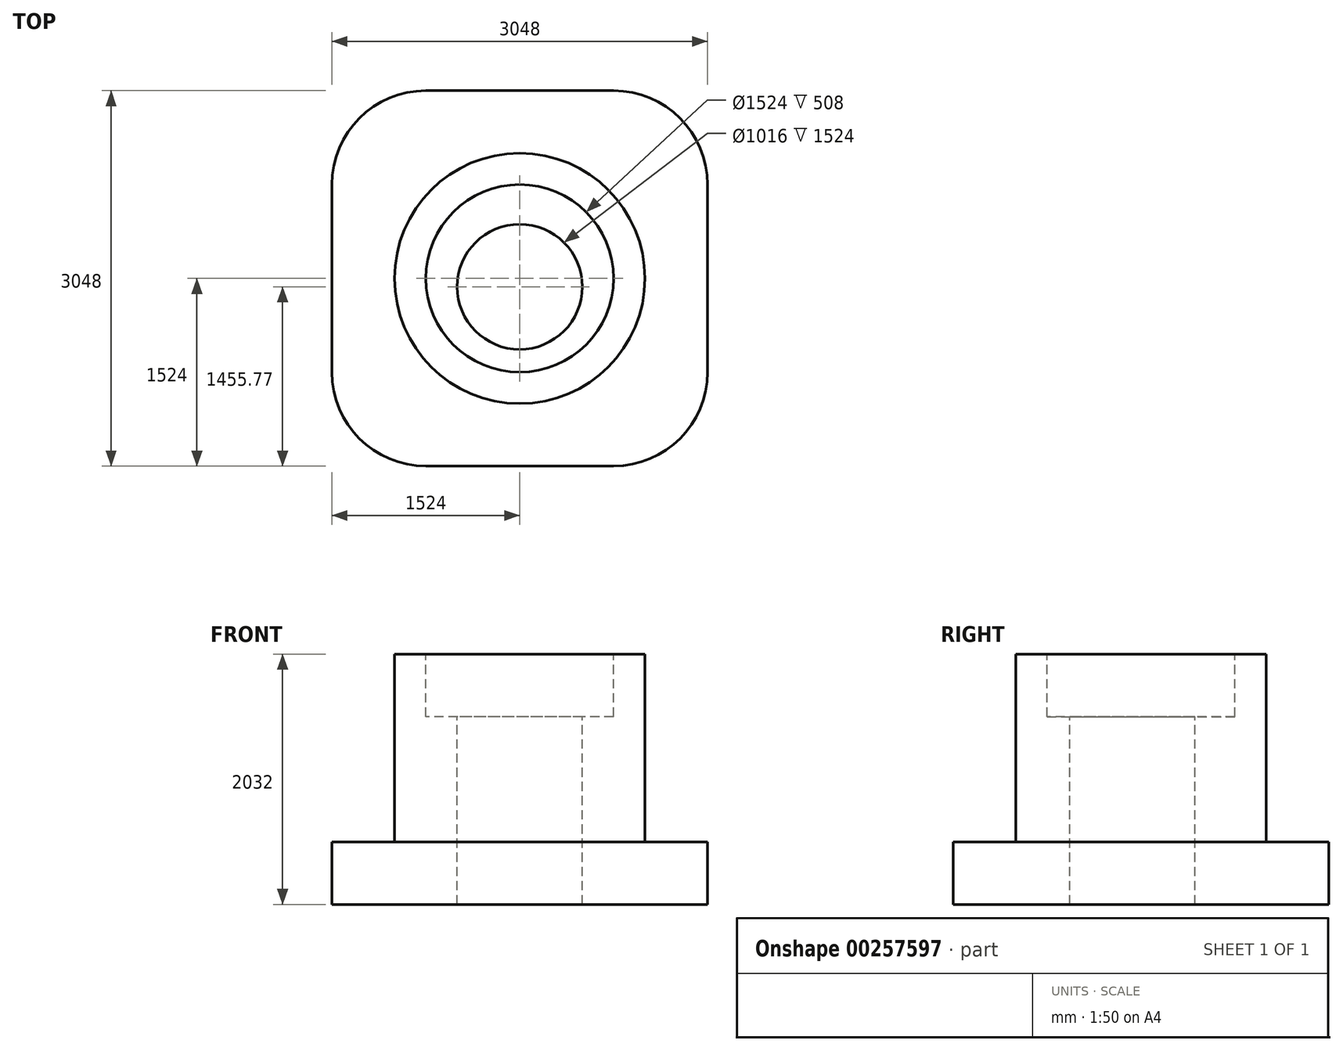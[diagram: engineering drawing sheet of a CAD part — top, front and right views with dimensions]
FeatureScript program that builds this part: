
annotation { "Feature Type Name" : "Feature", "Feature Type Description" : "" }
export const myFeature = defineFeature(function(context is Context, id is Id, definition is map)
    precondition{}
    {
        {
            var Q0;
            Q0=qCreatedBy(makeId("Top.planeOp"),FACE);
            var sketch = newSketch(context, id + "F0", { "sketchPlane" : qUnion([Q0])});
            skLineSegment(sketch, "E0.bottom", {"start": v(762, -1524) * mm, "end": v(-762, -1524) * mm});
            skLineSegment(sketch, "E0.top", {"start": v(762, 1524) * mm, "end": v(-762, 1524) * mm});
            skLineSegment(sketch, "E0.left", {"start": v(1524, -762) * mm, "end": v(1524, 762) * mm});
            skLineSegment(sketch, "E0.right", {"start": v(-1524, -762) * mm, "end": v(-1524, 762) * mm});
            skPoint(sketch, "E0.middle", {"position": v(0, 0) * mm});
            skPoint(sketch, "E1.visualSharp", {"position": v(-1524, 1524) * mm});
            skArc(sketch, "E1.filletArc", {"start": v(-762, 1524) * mm, "mid": v(-1300.82, 1300.82) * mm, "end": v(-1524, 762) * mm});
            skPoint(sketch, "E2.visualSharp", {"position": v(1524, 1524) * mm});
            skArc(sketch, "E2.filletArc", {"start": v(1524, 762) * mm, "mid": v(1300.82, 1300.82) * mm, "end": v(762, 1524) * mm});
            skPoint(sketch, "E3.visualSharp", {"position": v(1524, -1524) * mm});
            skArc(sketch, "E3.filletArc", {"start": v(762, -1524) * mm, "mid": v(1300.82, -1300.82) * mm, "end": v(1524, -762) * mm});
            skPoint(sketch, "E4.visualSharp", {"position": v(-1524, -1524) * mm});
            skArc(sketch, "E4.filletArc", {"start": v(-1524, -762) * mm, "mid": v(-1300.82, -1300.82) * mm, "end": v(-762, -1524) * mm});
            skSolve(sketch);
        }
        {
            var Q0;
            Q0=makeQuery(id+"F0.imprint","IMPRINT",FACE,{"disambiguationData":[TD([[makeQuery(id+"F0.imprint","IMPRINT",EDGE,{"derivedFrom":sQuery(id+"F0.wireOp",EDGE,"E0.bottom")}),-1.0]])]});
            extrude(context, id + "F1", {"entities" : qUnion([Q0]), "oppositeDirection" : true, "depth" : 508 * mm});
        }
        {
            var Q0;
            Q0=makeQuery(id+"F1.opExtrude","CAP_FACE",FACE,{"disambiguationData":[OSD([sQuery(id+"F0.wireOp",EDGE,"E0.bottom"),sQuery(id+"F0.wireOp",EDGE,"E0.top"),sQuery(id+"F0.wireOp",EDGE,"E0.left"),sQuery(id+"F0.wireOp",EDGE,"E0.right"),sQuery(id+"F0.wireOp",EDGE,"E1.filletArc"),sQuery(id+"F0.wireOp",EDGE,"E2.filletArc"),sQuery(id+"F0.wireOp",EDGE,"E3.filletArc"),sQuery(id+"F0.wireOp",EDGE,"E4.filletArc")])],"isStart":true});
            var sketch = newSketch(context, id + "F2", { "sketchPlane" : qUnion([Q0])});
            skCircle(sketch, "E5", {"center": v(0, 0) * mm, "radius": 1016 * mm});
            skSolve(sketch);
        }
        {
            var Q0;
            Q0 = qSketchRegion(id + "F2", true);
            extrude(context, id + "F3", {"entities" : qUnion([Q0]), "operationType" : NewBodyOperationType.ADD, "depth" : 1524 * mm});
        }
        {
            var Q0;
            Q0=makeQuery(id+"F3.opExtrude","CAP_FACE",FACE,{"disambiguationData":[OSD([sQuery(id+"F2.wireOp",EDGE,"E5")])],"isStart":false});
            var sketch = newSketch(context, id + "F4", { "sketchPlane" : qUnion([Q0])});
            skCircle(sketch, "E6", {"center": v(0, 0) * mm, "radius": 762 * mm});
            skSolve(sketch);
        }
        {
            var Q0;
            Q0 = qSketchRegion(id + "F4", true);
            extrude(context, id + "F5", {"entities" : qUnion([Q0]), "operationType" : NewBodyOperationType.REMOVE, "oppositeDirection" : true, "depth" : 508 * mm});
        }
        {
            var Q0;
            Q0=makeQuery(id+"F5.boolean.opBoolean","COPY",FACE,{"derivedFrom":makeQuery(id+"F5.opExtrude","CAP_FACE",FACE,{"disambiguationData":[OSD([sQuery(id+"F4.wireOp",EDGE,"E6")])],"isStart":false})});
            var sketch = newSketch(context, id + "F6", { "sketchPlane" : qUnion([Q0])});
            skCircle(sketch, "E7", {"center": v(0, -68.23) * mm, "radius": 508 * mm});
            skSolve(sketch);
        }
        {
            var Q0;
            Q0 = qSketchRegion(id + "F6", true);
            extrude(context, id + "F7", {"entities" : qUnion([Q0]), "operationType" : NewBodyOperationType.REMOVE, "oppositeDirection" : true, "depth" : 2032 * mm});
        }
    });
